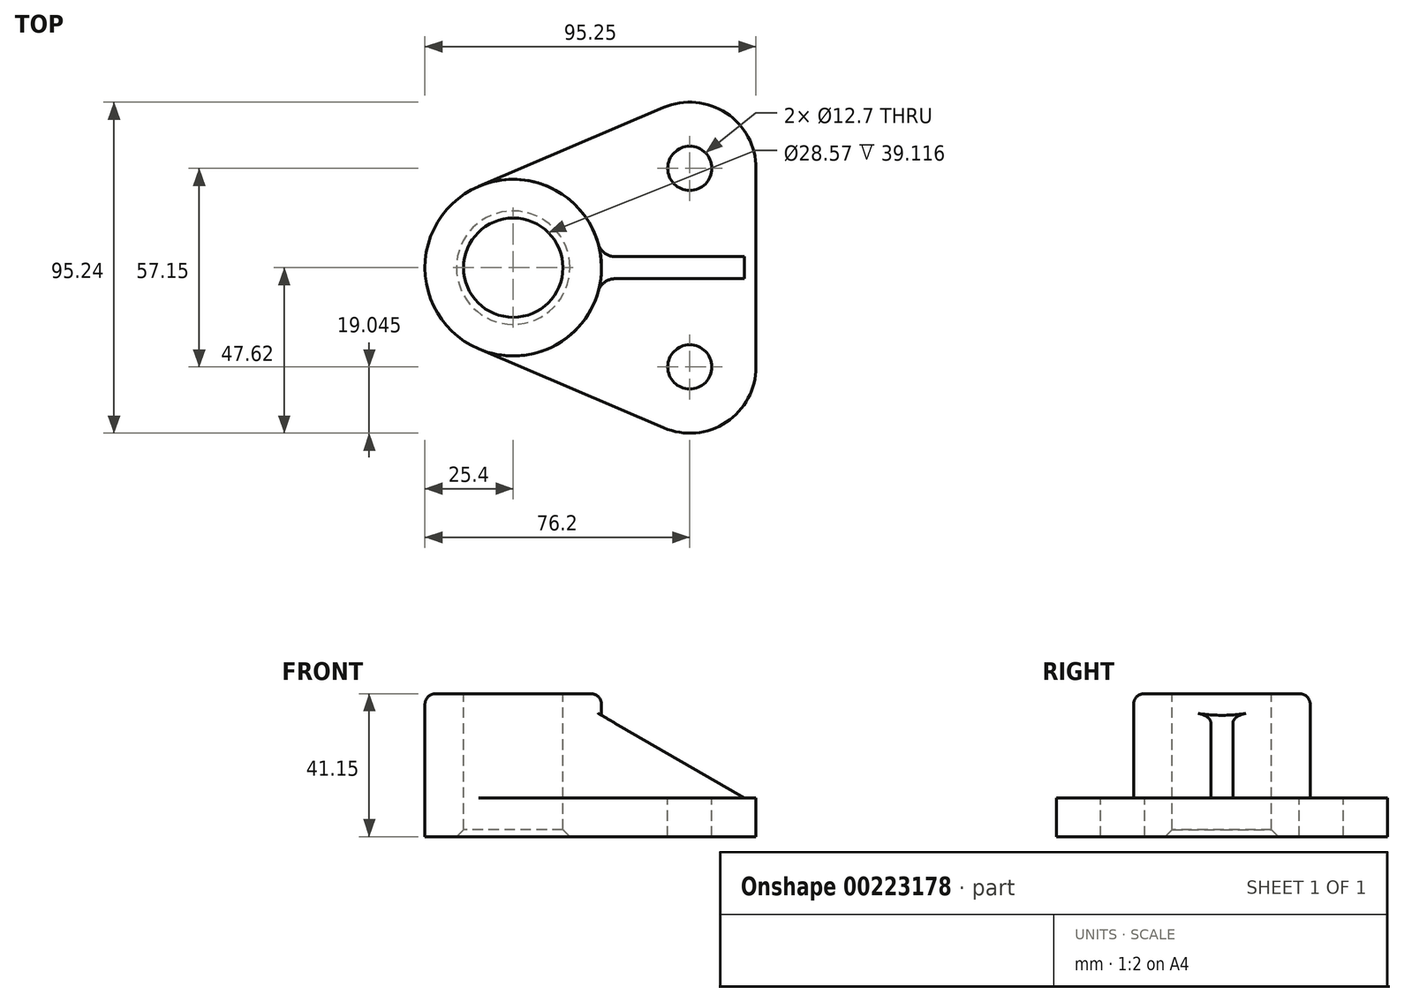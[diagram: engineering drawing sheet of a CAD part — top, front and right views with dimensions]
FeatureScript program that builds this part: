
annotation { "Feature Type Name" : "Feature", "Feature Type Description" : "" }
export const myFeature = defineFeature(function(context is Context, id is Id, definition is map)
    precondition{}
    {
        {
            var Q0;
            Q0=qCreatedBy(makeId("Top.planeOp"),FACE);
            var sketch = newSketch(context, id + "F0", { "sketchPlane" : qUnion([Q0])});
            skCircle(sketch, "E0", {"center": v(0, 0) * mm, "radius": 25.4 * mm});
            skLineSegment(sketch, "E1", {"start": v(0, 0) * mm, "end": v(100.04, 0) * mm, "construction": true});
            skLineSegment(sketch, "E2", {"start": v(-9.97, -23.36) * mm, "end": v(43.33, -46.1) * mm});
            skLineSegment(sketch, "E3", {"start": v(69.85, -28.58) * mm, "end": v(69.85, 28.58) * mm});
            skLineSegment(sketch, "E4", {"start": v(43.33, 46.1) * mm, "end": v(-9.97, 23.36) * mm});
            skPoint(sketch, "E5.visualSharp", {"position": v(69.85, 57.41) * mm});
            skArc(sketch, "E5.filletArc", {"start": v(69.85, 28.58) * mm, "mid": v(61.3, 44.47) * mm, "end": v(43.33, 46.1) * mm});
            skPoint(sketch, "E6.visualSharp", {"position": v(69.85, -57.41) * mm});
            skArc(sketch, "E6.filletArc", {"start": v(43.33, -46.1) * mm, "mid": v(61.3, -44.47) * mm, "end": v(69.85, -28.58) * mm});
            skSolve(sketch);
        }
        {
            var Q0;
            {var subQ1=sQuery(id+"F0.wireOp",EDGE,"E2");Q0=makeQuery(id+"F0.imprint","IMPRINT",FACE,{"disambiguationData":[TD([[makeQuery(id+"F0.imprint","IMPRINT",EDGE,{"derivedFrom":subQ1}),1.0]])]});}
            extrude(context, id + "F1", {"entities" : qUnion([Q0]), "depth" : 11.18 * mm});
        }
        {
            var Q0;
            {var subQ0=sQuery(id+"F0.wireOp",EDGE,"E0");var subQ1=makeQuery(id+"F0.imprint","INTERSECT",VERTEX,{"derivedFrom":[subQ0,sQuery(id+"F0.wireOp",EDGE,"E2")]});Q0=makeQuery(id+"F0.imprint","IMPRINT",FACE,{"disambiguationData":[TD([[makeQuery(id+"F0.imprint","IMPRINT",EDGE,{"disambiguationData":[TD([[subQ1,1.0]])],"derivedFrom":subQ0}),1.0]])]});}
            extrude(context, id + "F2", {"entities" : qUnion([Q0]), "operationType" : NewBodyOperationType.ADD, "depth" : 41.15 * mm});
        }
        {
            var Q0;
            Q0=makeQuery(id+"F2.opExtrude","CAP_FACE",FACE,{"disambiguationData":[OSD([sQuery(id+"F0.wireOp",EDGE,"E0")])],"isStart":false});
            var sketch = newSketch(context, id + "F3", { "sketchPlane" : qUnion([Q0])});
            skCircle(sketch, "E7", {"center": v(0, 0) * mm, "radius": 14.29 * mm});
            skSolve(sketch);
        }
        {
            var Q0;
            Q0 = qSketchRegion(id + "F3", true);
            extrude(context, id + "F4", {"entities" : qUnion([Q0]), "operationType" : NewBodyOperationType.REMOVE, "endBound" : BoundingType.THROUGH_ALL, "oppositeDirection" : true, "depth" : 25.4 * mm});
        }
        {
            var Q0;
            Q0=makeQuery(id+"F1.opExtrude","CAP_FACE",FACE,{"disambiguationData":[OSD([sQuery(id+"F0.wireOp",EDGE,"E0"),sQuery(id+"F0.wireOp",EDGE,"E2"),sQuery(id+"F0.wireOp",EDGE,"E3"),sQuery(id+"F0.wireOp",EDGE,"E4"),sQuery(id+"F0.wireOp",EDGE,"E5.filletArc"),sQuery(id+"F0.wireOp",EDGE,"E6.filletArc")])],"isStart":false});
            var sketch = newSketch(context, id + "F5", { "sketchPlane" : qUnion([Q0])});
            skCircle(sketch, "E8", {"center": v(50.8, 28.58) * mm, "radius": 6.35 * mm});
            skCircle(sketch, "E9", {"center": v(50.8, -28.58) * mm, "radius": 6.35 * mm});
            skSolve(sketch);
        }
        {
            var Q0;
            Q0 = qSketchRegion(id + "F5", true);
            extrude(context, id + "F6", {"entities" : qUnion([Q0]), "operationType" : NewBodyOperationType.REMOVE, "endBound" : BoundingType.THROUGH_ALL, "oppositeDirection" : true, "depth" : 25.4 * mm});
        }
        {
            var Q0;
            Q0=qCreatedBy(makeId("Front.planeOp"),FACE);
            var sketch = newSketch(context, id + "F7", { "sketchPlane" : qUnion([Q0])});
            skLineSegment(sketch, "E10.0.1", {"start": v(66.55, 11.18) * mm, "end": v(43.33, 11.18) * mm});
            skLineSegment(sketch, "E10.0.2", {"start": v(43.33, 11.18) * mm, "end": v(25.4, 11.18) * mm});
            skLineSegment(sketch, "E10.0.4", {"start": v(25.4, 11.18) * mm, "end": v(43.33, 11.18) * mm});
            skLineSegment(sketch, "E10.0.5", {"start": v(43.33, 11.18) * mm, "end": v(66.55, 11.18) * mm});
            skLineSegment(sketch, "E11", {"start": v(25.42, 34.92) * mm, "end": v(66.55, 11.18) * mm});
            skPoint(sketch, "E10.0.3.end.orphan", {"position": v(25.4, 11.18) * mm});
            skLineSegment(sketch, "E12", {"start": v(25.4, 11.18) * mm, "end": v(22.55, 11.18) * mm});
            skLineSegment(sketch, "E13", {"start": v(22.55, 11.18) * mm, "end": v(22.55, 36.58) * mm});
            skLineSegment(sketch, "E14", {"start": v(22.55, 36.58) * mm, "end": v(25.42, 34.92) * mm});
            skSolve(sketch);
        }
        {
            var Q0;
            Q0 = qSketchRegion(id + "F7", true);
            extrude(context, id + "F8", {"entities" : qUnion([Q0]), "operationType" : NewBodyOperationType.ADD, "endBound" : BoundingType.SYMMETRIC, "depth" : 6.35 * mm});
        }
        {
            var Q0;
            Q0=makeQuery(id+"F4.boolean.opBoolean","COPY",EDGE,{"derivedFrom":makeQuery(id+"F4.opExtrude","CAP_EDGE",EDGE,{"disambiguationData":[OSD([sQuery(id+"F3.wireOp",EDGE,"E7")])],"isStart":true})});
            var Q1;
            {var subQ0=sQuery(id+"F0.wireOp",EDGE,"E0");Q1=makeQuery(id+"F4.boolean.opBoolean","INTERSECT",EDGE,{"derivedFrom":[makeQuery(id+"F2.boolean.opBoolean","MERGE",FACE,{"derivedFrom":[makeQuery(id+"F1.opExtrude","CAP_FACE",FACE,{"disambiguationData":[OSD([subQ0,sQuery(id+"F0.wireOp",EDGE,"E2"),sQuery(id+"F0.wireOp",EDGE,"E3"),sQuery(id+"F0.wireOp",EDGE,"E4"),sQuery(id+"F0.wireOp",EDGE,"E5.filletArc"),sQuery(id+"F0.wireOp",EDGE,"E6.filletArc")])],"isStart":true}),makeQuery(id+"F2.opExtrude","CAP_FACE",FACE,{"disambiguationData":[OSD([subQ0])],"isStart":true})]}),makeQuery(id+"F4.opExtrude","SWEPT_FACE",FACE,{"disambiguationData":[OSD([sQuery(id+"F3.wireOp",EDGE,"E7")])]})]});}
            chamfer(context, id + "F9", {"entities" : qUnion([Q0, Q1]), "chamferType" : ChamferType.OFFSET_ANGLE, "width" : 2.03 * mm, "oppositeDirection" : false, "angle" : 45 * degree, "tangentPropagation" : true});
        }
        {
            var Q0;
            Q0=makeQuery(id+"F2.opExtrude","CAP_EDGE",EDGE,{"disambiguationData":[OSD([sQuery(id+"F0.wireOp",EDGE,"E0")])],"isStart":false});
            fillet(context, id + "F10", {"entities" : qUnion([Q0]), "radius" : 3.05 * mm, "tangentPropagation" : true, "allowEdgeOverflow" : false});
        }
        {
            var Q0;
            {var subQ0=sQuery(id+"F0.wireOp",EDGE,"E2");var subQ1=sQuery(id+"F0.wireOp",EDGE,"E0");Q0=makeQuery(id+"F8.boolean.opBoolean","SPLIT",EDGE,{"disambiguationData":[TD([makeQuery(id+"F1.opExtrude","SWEPT_FACE",FACE,{"disambiguationData":[OSD([subQ0])]})])],"derivedFrom":makeQuery(id+"F1.opExtrude","CAP_EDGE",EDGE,{"disambiguationData":[OSD([subQ1])],"isStart":false})});}
            var Q1;
            Q1=makeQuery(id+"F8.boolean.opBoolean","INTERSECT",EDGE,{"derivedFrom":[makeQuery(id+"F2.opExtrude","SWEPT_FACE",FACE,{"disambiguationData":[OSD([sQuery(id+"F0.wireOp",EDGE,"E0")])]}),makeQuery(id+"F8.opExtrude","CAP_FACE",FACE,{"disambiguationData":[OSD([sQuery(id+"F7.wireOp",EDGE,"E10.0.4"),sQuery(id+"F7.wireOp",EDGE,"E10.0.5"),sQuery(id+"F7.wireOp",EDGE,"E11"),sQuery(id+"F7.wireOp",EDGE,"E12"),sQuery(id+"F7.wireOp",EDGE,"E13"),sQuery(id+"F7.wireOp",EDGE,"E14")])],"isStart":false})]});
            var Q2;
            Q2=makeQuery(id+"F8.opExtrude","CAP_EDGE",EDGE,{"disambiguationData":[OSD([sQuery(id+"F7.wireOp",EDGE,"E10.0.4"),sQuery(id+"F7.wireOp",EDGE,"E10.0.5"),sQuery(id+"F7.wireOp",EDGE,"E12")])],"isStart":false});
            var Q3;
            Q3=makeQuery(id+"F8.opExtrude","CAP_EDGE",EDGE,{"disambiguationData":[OSD([sQuery(id+"F7.wireOp",EDGE,"E10.0.4"),sQuery(id+"F7.wireOp",EDGE,"E10.0.5"),sQuery(id+"F7.wireOp",EDGE,"E12")])],"isStart":true});
            var Q4;
            Q4=makeQuery(id+"F8.boolean.opBoolean","INTERSECT",EDGE,{"derivedFrom":[makeQuery(id+"F2.opExtrude","SWEPT_FACE",FACE,{"disambiguationData":[OSD([sQuery(id+"F0.wireOp",EDGE,"E0")])]}),makeQuery(id+"F8.opExtrude","CAP_FACE",FACE,{"disambiguationData":[OSD([sQuery(id+"F7.wireOp",EDGE,"E10.0.4"),sQuery(id+"F7.wireOp",EDGE,"E10.0.5"),sQuery(id+"F7.wireOp",EDGE,"E11"),sQuery(id+"F7.wireOp",EDGE,"E12"),sQuery(id+"F7.wireOp",EDGE,"E13"),sQuery(id+"F7.wireOp",EDGE,"E14")])],"isStart":true})]});
            var Q5;
            {var subQ0=sQuery(id+"F0.wireOp",EDGE,"E4");var subQ1=sQuery(id+"F0.wireOp",EDGE,"E0");Q5=makeQuery(id+"F8.boolean.opBoolean","SPLIT",EDGE,{"disambiguationData":[TD([makeQuery(id+"F1.opExtrude","SWEPT_FACE",FACE,{"disambiguationData":[OSD([subQ0])]})])],"derivedFrom":makeQuery(id+"F1.opExtrude","CAP_EDGE",EDGE,{"disambiguationData":[OSD([subQ1])],"isStart":false})});}
            fillet(context, id + "F11", {"entities" : qUnion([Q0, Q1, Q2, Q3, Q4, Q5]), "radius" : 5.08 * mm, "tangentPropagation" : true, "allowEdgeOverflow" : false});
        }
    });
